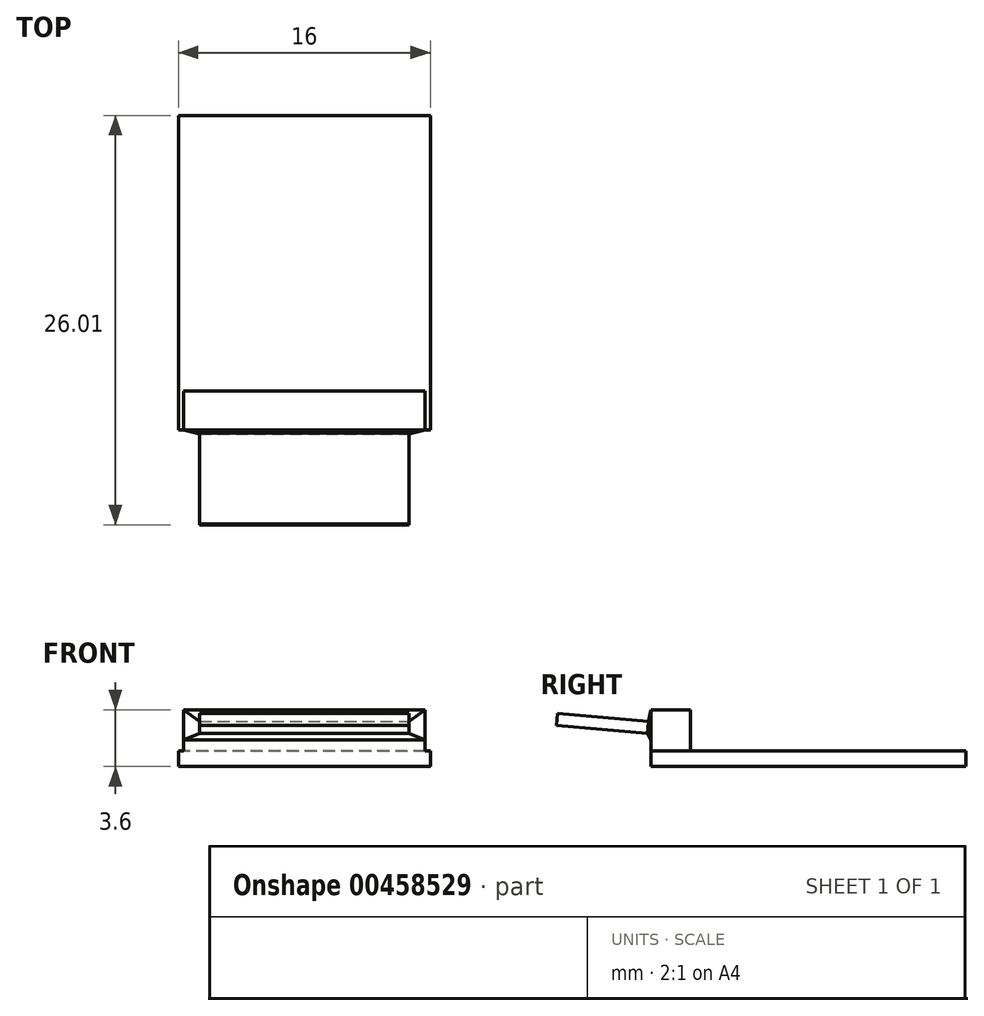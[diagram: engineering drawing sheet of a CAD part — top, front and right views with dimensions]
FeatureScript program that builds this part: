
annotation { "Feature Type Name" : "Feature", "Feature Type Description" : "" }
export const myFeature = defineFeature(function(context is Context, id is Id, definition is map)
    precondition{}
    {
        {
            var Q0;
            Q0=qCreatedBy(makeId("Top.planeOp"),FACE);
            var sketch = newSketch(context, id + "F0", { "sketchPlane" : qUnion([Q0])});
            skLineSegment(sketch, "E0.bottom", {"start": v(-8, 10) * mm, "end": v(8, 10) * mm});
            skLineSegment(sketch, "E0.top", {"start": v(-8, -10) * mm, "end": v(8, -10) * mm});
            skLineSegment(sketch, "E0.left", {"start": v(-8, 10) * mm, "end": v(-8, -10) * mm});
            skLineSegment(sketch, "E0.right", {"start": v(8, 10) * mm, "end": v(8, -10) * mm});
            skPoint(sketch, "E0.middle", {"position": v(0, 0) * mm});
            skSolve(sketch);
        }
        {
            var Q0;
            Q0=qSketchRegion(id+"F0",true);
            extrude(context, id + "F1", {"entities" : qUnion([Q0]), "depth" : 1 * mm});
        }
        {
            var Q0;
            Q0=makeQuery(id+"F1.opExtrude","CAP_FACE",FACE,{"disambiguationData":[OSD([sQuery(id+"F0.wireOp",EDGE,"E0.bottom"),sQuery(id+"F0.wireOp",EDGE,"E0.top"),sQuery(id+"F0.wireOp",EDGE,"E0.left"),sQuery(id+"F0.wireOp",EDGE,"E0.right")])],"isStart":false});
            var sketch = newSketch(context, id + "F2", { "sketchPlane" : qUnion([Q0])});
            skLineSegment(sketch, "E1.bottom", {"start": v(7.68, -10) * mm, "end": v(-7.67, -10) * mm});
            skLineSegment(sketch, "E1.top", {"start": v(7.68, -7.5) * mm, "end": v(-7.67, -7.5) * mm});
            skLineSegment(sketch, "E1.left", {"start": v(7.68, -10) * mm, "end": v(7.68, -7.5) * mm});
            skLineSegment(sketch, "E1.right", {"start": v(-7.67, -10) * mm, "end": v(-7.67, -7.5) * mm});
            skPoint(sketch, "E1.middle", {"position": v(0, -8.75) * mm});
            skSolve(sketch);
        }
        {
            var Q0;
            Q0=makeQuery(id+"F2.imprint","IMPRINT",FACE,{"disambiguationData":[TD([[makeQuery(id+"F2.imprint","IMPRINT",EDGE,{"derivedFrom":sQuery(id+"F2.wireOp",EDGE,"E1.bottom")}),1.0]])]});
            extrude(context, id + "F3", {"entities" : qUnion([Q0]), "operationType" : NewBodyOperationType.ADD, "depth" : 2.6 * mm});
        }
        {
            var Q0;
            Q0=makeQuery(id+"F3.boolean.opBoolean","MERGE",FACE,{"derivedFrom":[makeQuery(id+"F1.opExtrude","SWEPT_FACE",FACE,{"disambiguationData":[OSD([sQuery(id+"F0.wireOp",EDGE,"E0.top")])]}),makeQuery(id+"F3.opExtrude","SWEPT_FACE",FACE,{"disambiguationData":[OSD([sQuery(id+"F2.wireOp",EDGE,"E1.bottom")])]})]});
            var sketch = newSketch(context, id + "F4", { "sketchPlane" : qUnion([Q0])});
            skLineSegment(sketch, "E2", {"start": v(-7.67, 1.7) * mm, "end": v(7.67, 1.7) * mm});
            skSolve(sketch);
        }
        {
            var Q0;
            Q0=makeQuery(id+"F3.opExtrude","CAP_EDGE",EDGE,{"disambiguationData":[OSD([sQuery(id+"F2.wireOp",EDGE,"E1.bottom")])],"isStart":false});
            var Q1;
            {var subQ0=sQuery(id+"F4.wireOp",EDGE,"E2");Q1=makeQuery(id+"F4.imprint","IMPRINT",FACE,{"disambiguationData":[TD([[makeQuery(id+"F4.imprint","IMPRINT",EDGE,{"derivedFrom":subQ0}),1.0]])]});}
            cPlane(context, id + "F5", {"entities" : qUnion([Q0, Q1]), "cplaneType" : CPlaneType.LINE_ANGLE, "offset" : 25 * mm, "angle" : 5 * degree, "oppositeDirection" : true, "width" : 150 * mm, "height" : 150 * mm});
        }
        {
            var Q0;
            Q0=qCreatedBy(id+"F5.planeOp",FACE);
            cPlane(context, id + "F6", {"entities" : qUnion([Q0]), "cplaneType" : CPlaneType.OFFSET, "offset" : 0.1 * mm, "oppositeDirection" : true, "width" : 150 * mm, "height" : 150 * mm});
        }
        {
            var Q0;
            Q0=qCreatedBy(id+"F6.planeOp",FACE);
            var sketch = newSketch(context, id + "F7", { "sketchPlane" : qUnion([Q0])});
            skLineSegment(sketch, "E3.bottom", {"start": v(6.65, 1.96) * mm, "end": v(-6.65, 1.96) * mm});
            skLineSegment(sketch, "E3.top", {"start": v(6.65, 1.21) * mm, "end": v(-6.65, 1.21) * mm});
            skLineSegment(sketch, "E3.left", {"start": v(6.65, 1.96) * mm, "end": v(6.65, 1.21) * mm});
            skLineSegment(sketch, "E3.right", {"start": v(-6.65, 1.96) * mm, "end": v(-6.65, 1.21) * mm});
            skPoint(sketch, "E3.middle", {"position": v(0, 1.59) * mm});
            skSolve(sketch);
        }
        {
            var Q0;
            Q0=makeQuery(id+"F7.imprint","IMPRINT",FACE,{"disambiguationData":[TD([[makeQuery(id+"F7.imprint","IMPRINT",EDGE,{"derivedFrom":sQuery(id+"F7.wireOp",EDGE,"E3.bottom")}),1.0]])]});
            extrude(context, id + "F8", {"entities" : qUnion([Q0]), "oppositeDirection" : true, "depth" : 5.8 * mm});
        }
        {
            var Q2;
            {var subQ0=sQuery(id+"F4.wireOp",EDGE,"E2");Q2=makeQuery(id+"F4.imprint","IMPRINT",FACE,{"disambiguationData":[TD([[makeQuery(id+"F4.imprint","IMPRINT",EDGE,{"derivedFrom":subQ0}),1.0]])]});}
            var Q3;
            Q3=makeQuery(id+"F8.opExtrude","CAP_FACE",FACE,{"disambiguationData":[OSD([sQuery(id+"F7.wireOp",EDGE,"E3.bottom"),sQuery(id+"F7.wireOp",EDGE,"E3.top"),sQuery(id+"F7.wireOp",EDGE,"E3.left"),sQuery(id+"F7.wireOp",EDGE,"E3.right")])],"isStart":true});
            loft(context, id + "F9", {"operationType" : NewBodyOperationType.ADD, "sheetProfilesArray" : [{ "sheetProfileEntities" : qUnion([Q2]) }, { "sheetProfileEntities" : qUnion([Q3]) }]});
        }
    });
